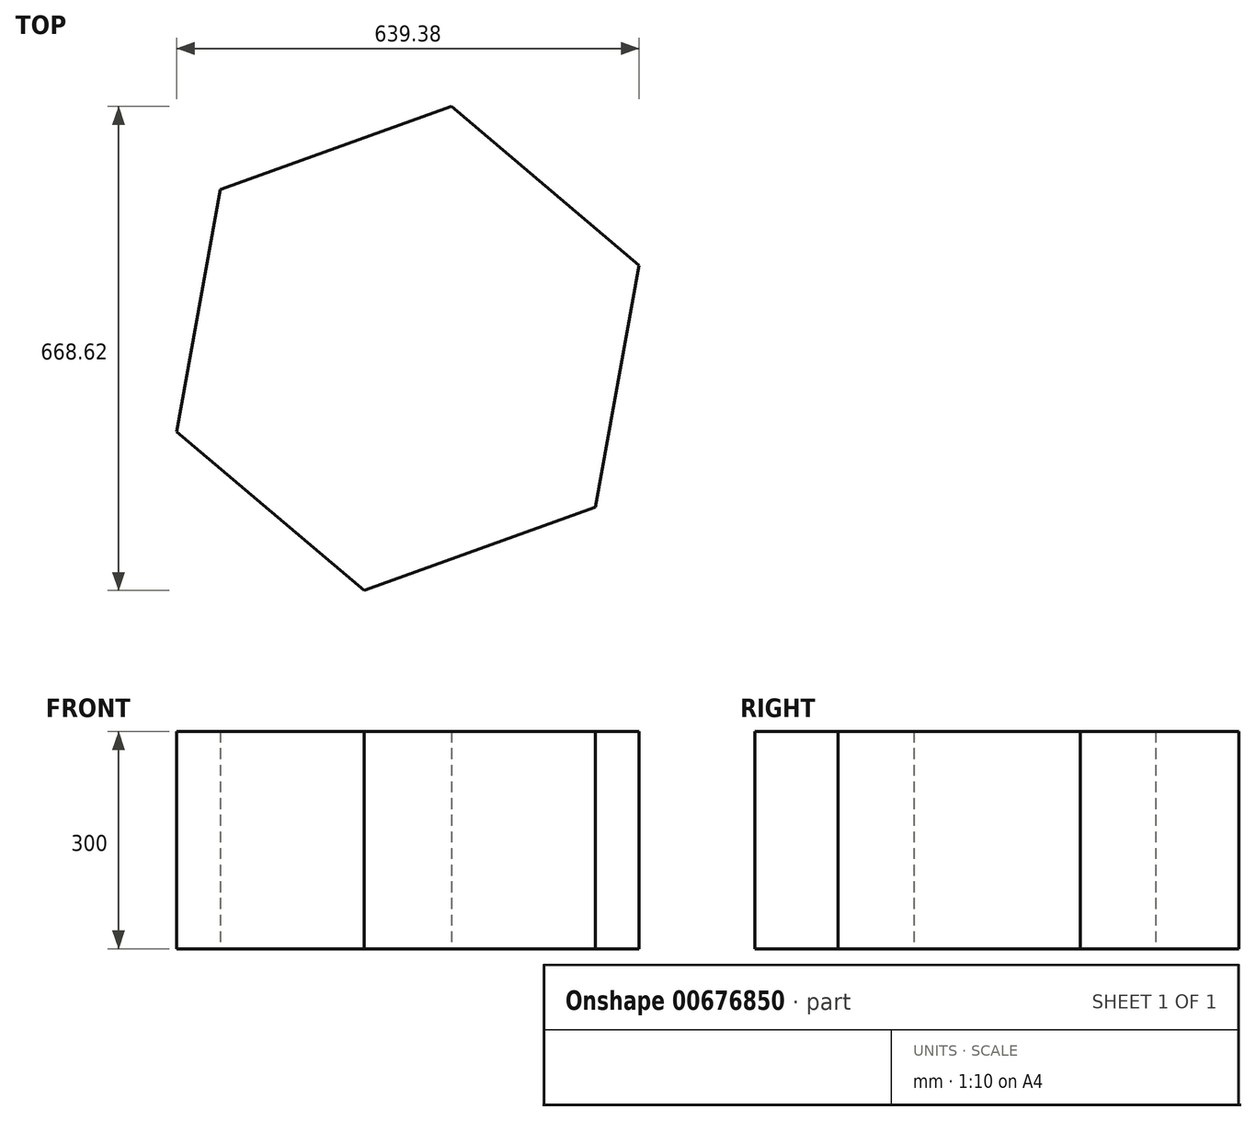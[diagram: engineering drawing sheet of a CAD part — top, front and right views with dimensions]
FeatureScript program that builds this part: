
annotation { "Feature Type Name" : "Feature", "Feature Type Description" : "" }
export const myFeature = defineFeature(function(context is Context, id is Id, definition is map)
    precondition{}
    {
        {
            var Q0;
            Q0=qCreatedBy(makeId("Top.planeOp"),FACE);
            var sketch = newSketch(context, id + "F0", { "sketchPlane" : qUnion([Q0])});
            skCircle(sketch, "E0.cCircle", {"center": v(0, 0) * mm, "radius": 294.2 * mm, "construction": true});
            skLineSegment(sketch, "E0.0", {"start": v(319.69, 114.9) * mm, "end": v(259.35, -219.4) * mm});
            skLineSegment(sketch, "E0.1", {"start": v(259.35, -219.4) * mm, "end": v(-60.34, -334.3) * mm});
            skLineSegment(sketch, "E0.2", {"start": v(-60.34, -334.3) * mm, "end": v(-319.69, -114.9) * mm});
            skLineSegment(sketch, "E0.3", {"start": v(-319.69, -114.9) * mm, "end": v(-259.35, 219.4) * mm});
            skLineSegment(sketch, "E0.4", {"start": v(-259.35, 219.4) * mm, "end": v(60.34, 334.3) * mm});
            skLineSegment(sketch, "E0.5", {"start": v(60.34, 334.3) * mm, "end": v(319.69, 114.9) * mm});
            skPoint(sketch, "E0.0.midPoint", {"position": v(289.52, -52.25) * mm});
            skSolve(sketch);
        }
        {
            var Q0;
            Q0=makeQuery(id+"F0.imprint","IMPRINT",FACE,{"disambiguationData":[TD([[makeQuery(id+"F0.imprint","IMPRINT",EDGE,{"derivedFrom":sQuery(id+"F0.wireOp",EDGE,"E0.0")}),-1.0]])]});
            extrude(context, id + "F1", {"entities" : qUnion([Q0]), "depth" : 300 * mm, "offsetDistance" : 25 * mm});
        }
    });
